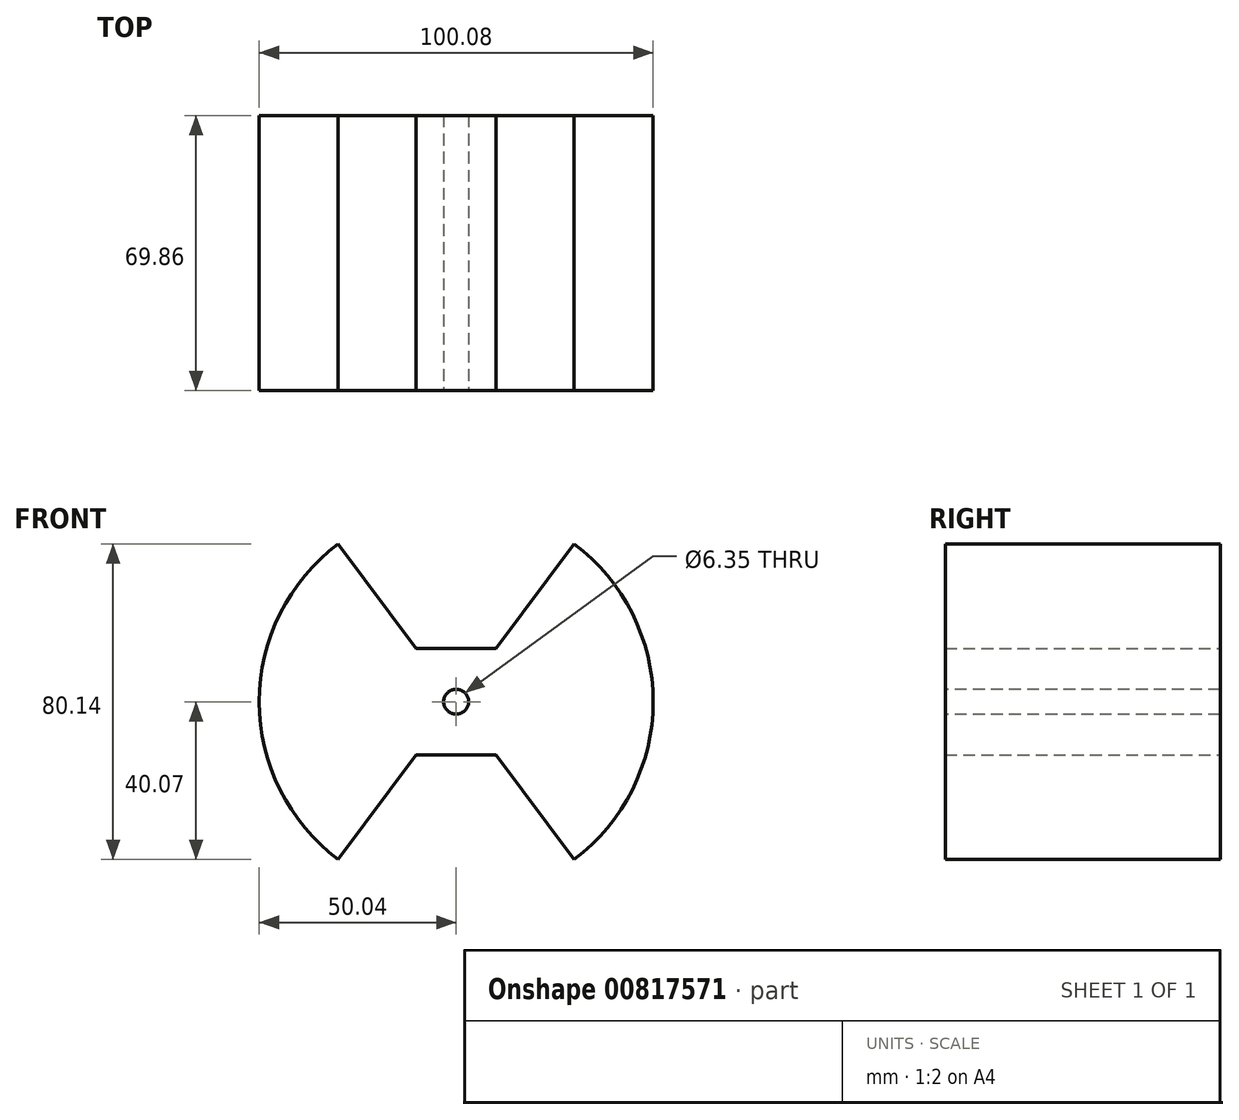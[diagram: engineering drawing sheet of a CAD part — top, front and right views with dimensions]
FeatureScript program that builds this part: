
annotation { "Feature Type Name" : "Feature", "Feature Type Description" : "" }
export const myFeature = defineFeature(function(context is Context, id is Id, definition is map)
    precondition{}
    {
        {
            var Q0;
            Q0=qCreatedBy(makeId("Front.planeOp"),FACE);
            var sketch = newSketch(context, id + "F0", { "sketchPlane" : qUnion([Q0])});
            skCircle(sketch, "E0", {"center": v(0, 0) * mm, "radius": 50.04 * mm});
            skLineSegment(sketch, "E1", {"start": v(-29.97, 40.07) * mm, "end": v(0, 0) * mm});
            skLineSegment(sketch, "E2", {"start": v(0, 0) * mm, "end": v(29.97, 40.07) * mm});
            skLineSegment(sketch, "E3", {"start": v(0, 0) * mm, "end": v(29.97, -40.07) * mm});
            skLineSegment(sketch, "E4", {"start": v(0, 0) * mm, "end": v(-29.97, -40.07) * mm});
            skLineSegment(sketch, "E5", {"start": v(-10.16, 13.59) * mm, "end": v(10.16, 13.59) * mm});
            skLineSegment(sketch, "E6", {"start": v(-10.16, -13.58) * mm, "end": v(10.16, -13.58) * mm});
            skSolve(sketch);
        }
        {
            var Q0;
            {var subQ3=sQuery(id+"F0.wireOp",EDGE,"E5");Q0=makeQuery(id+"F0.imprint","IMPRINT",FACE,{"disambiguationData":[TD([[makeQuery(id+"F0.imprint","IMPRINT",EDGE,{"derivedFrom":subQ3}),-1.0]])]});}
            var Q1;
            {var subQ3=sQuery(id+"F0.wireOp",EDGE,"E6");Q1=makeQuery(id+"F0.imprint","IMPRINT",FACE,{"disambiguationData":[TD([[makeQuery(id+"F0.imprint","IMPRINT",EDGE,{"derivedFrom":subQ3}),1.0]])]});}
            var Q2;
            {var subQ0=sQuery(id+"F0.wireOp",EDGE,"E2");var subQ1=sQuery(id+"F0.wireOp",EDGE,"E0");var subQ2=makeQuery(id+"F0.imprint","INTERSECT",VERTEX,{"derivedFrom":[subQ1,subQ0]});Q2=makeQuery(id+"F0.imprint","IMPRINT",FACE,{"disambiguationData":[TD([[makeQuery(id+"F0.imprint","IMPRINT",EDGE,{"disambiguationData":[TD([[subQ2,1.0]])],"derivedFrom":subQ1}),1.0]])]});}
            var Q3;
            {var subQ1=sQuery(id+"F0.wireOp",EDGE,"E1");var subQ5=sQuery(id+"F0.wireOp",EDGE,"E0");var subQ6=makeQuery(id+"F0.imprint","INTERSECT",VERTEX,{"derivedFrom":[subQ5,subQ1]});Q3=makeQuery(id+"F0.imprint","IMPRINT",FACE,{"disambiguationData":[TD([[makeQuery(id+"F0.imprint","IMPRINT",EDGE,{"disambiguationData":[TD([[subQ6,-1.0]])],"derivedFrom":subQ5}),1.0]])]});}
            extrude(context, id + "F1", {"entities" : qUnion([Q0, Q1, Q2, Q3]), "endBound" : BoundingType.SYMMETRIC, "depth" : 69.85 * mm, "offsetDistance" : 25.4 * mm});
        }
        {
            var Q0;
            Q0=sQuery(id+"F0.wireOp",VERTEX,"E0.center");
            var Q1;
            Q1=makeQuery(id+"F1.opExtrude","SWEPT_BODY",BODY,{"disambiguationData":[OSD([sQuery(id+"F0.wireOp",EDGE,"E0"),sQuery(id+"F0.wireOp",EDGE,"E1"),sQuery(id+"F0.wireOp",EDGE,"E2"),sQuery(id+"F0.wireOp",EDGE,"E3"),sQuery(id+"F0.wireOp",EDGE,"E4"),sQuery(id+"F0.wireOp",EDGE,"E5"),sQuery(id+"F0.wireOp",EDGE,"E6")])]});
            hole(context, id + "F2", {"style" : HoleStyle.SIMPLE, "endStyle" : HoleEndStyle.THROUGH, "holeDiameter" : 3.56 * mm, "majorDiameter" : 6.35 * mm, "isTappedThrough" : true, "tappedDepth" : 12.7 * mm, "tapClearance" : 3, "locations" : qUnion([Q0]), "scope" : qUnion([Q1])});
        }
        {
            var Q0;
            Q0=qCreatedBy(makeId("Front.planeOp"),FACE);
            var sketch = newSketch(context, id + "F3", { "sketchPlane" : qUnion([Q0])});
            skCircle(sketch, "E7", {"center": v(0, 0) * mm, "radius": 3.18 * mm});
            skSolve(sketch);
        }
        {
            var Q0;
            Q0 = qSketchRegion(id + "F3", true);
            var Q1;
            Q1=makeQuery(id+"F1.opExtrude","CAP_FACE",FACE,{"disambiguationData":[OSD([sQuery(id+"F0.wireOp",EDGE,"E0"),sQuery(id+"F0.wireOp",EDGE,"E1"),sQuery(id+"F0.wireOp",EDGE,"E2"),sQuery(id+"F0.wireOp",EDGE,"E3"),sQuery(id+"F0.wireOp",EDGE,"E4"),sQuery(id+"F0.wireOp",EDGE,"E5"),sQuery(id+"F0.wireOp",EDGE,"E6")])],"isStart":false});
            var Q2;
            Q2=makeQuery(id+"F1.opExtrude","CAP_FACE",FACE,{"disambiguationData":[OSD([sQuery(id+"F0.wireOp",EDGE,"E0"),sQuery(id+"F0.wireOp",EDGE,"E1"),sQuery(id+"F0.wireOp",EDGE,"E2"),sQuery(id+"F0.wireOp",EDGE,"E3"),sQuery(id+"F0.wireOp",EDGE,"E4"),sQuery(id+"F0.wireOp",EDGE,"E5"),sQuery(id+"F0.wireOp",EDGE,"E6")])],"isStart":true});
            extrude(context, id + "F4", {"entities" : qUnion([Q0]), "operationType" : NewBodyOperationType.REMOVE, "endBound" : BoundingType.SYMMETRIC, "oppositeDirection" : true, "depth" : 69.85 * mm, "endBoundEntityFace" : qUnion([Q1]), "offsetDistance" : 0 * mm, "hasSecondDirection" : true, "secondDirectionBound" : SecondDirectionBoundingType.UP_TO_SURFACE, "secondDirectionOppositeDirection" : false, "secondDirectionDepth" : 25.4 * mm, "secondDirectionBoundEntityFace" : qUnion([Q2])});
        }
    });
